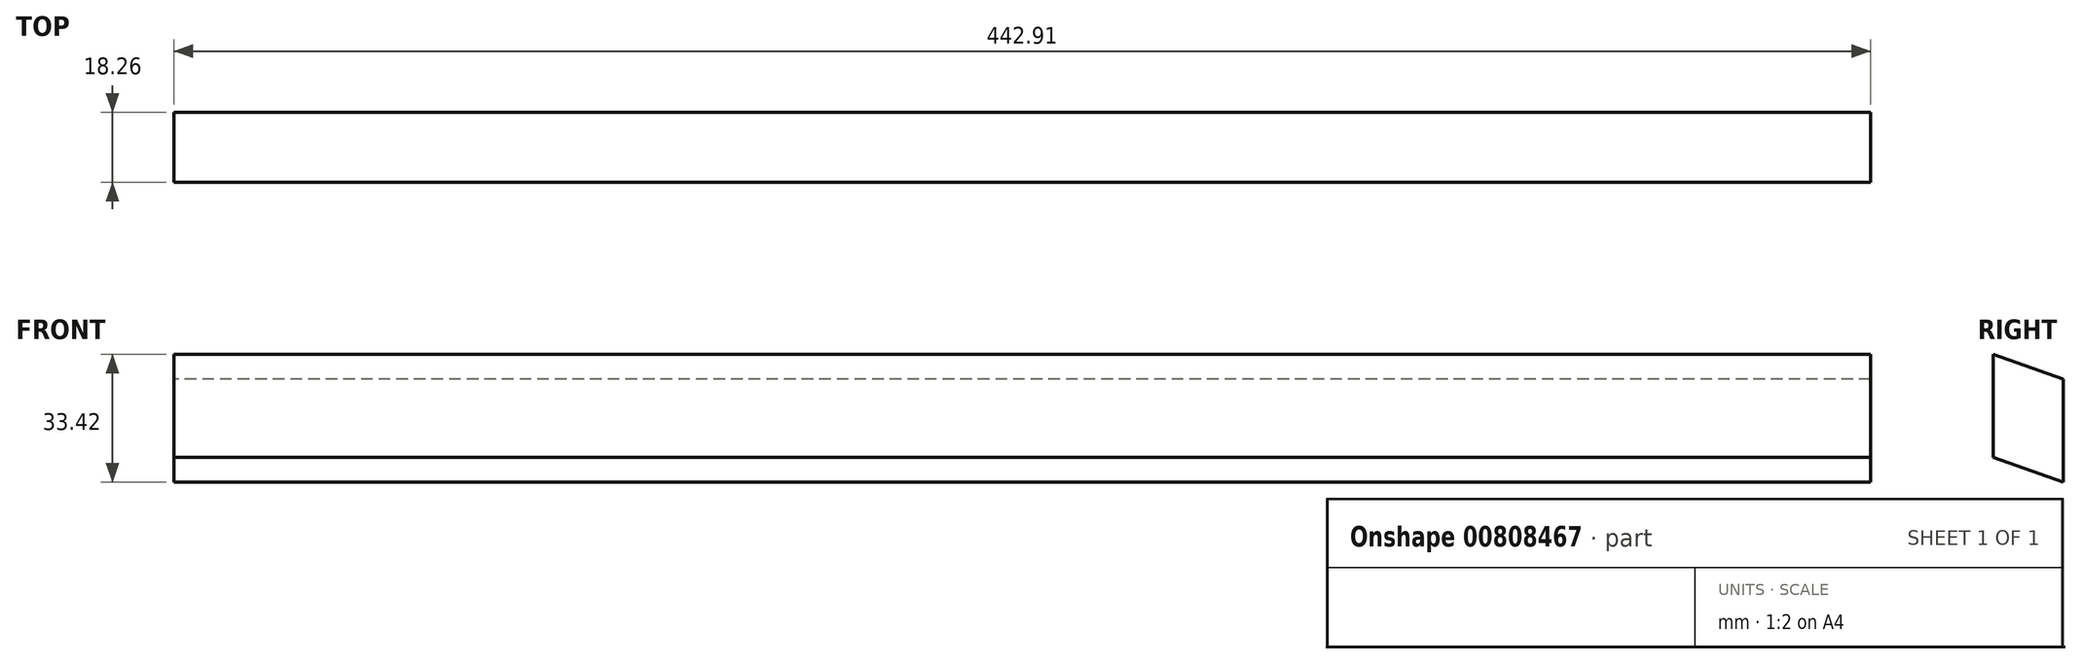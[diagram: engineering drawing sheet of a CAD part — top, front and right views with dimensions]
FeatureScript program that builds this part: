
annotation { "Feature Type Name" : "Feature", "Feature Type Description" : "" }
export const myFeature = defineFeature(function(context is Context, id is Id, definition is map)
    precondition{}
    {
        {
            var Q0;
            Q0=qCreatedBy(makeId("Right.planeOp"),FACE);
            var sketch = newSketch(context, id + "F0", { "sketchPlane" : qUnion([Q0])});
            skLineSegment(sketch, "E0", {"start": v(-140.85, 19.98) * mm, "end": v(-140.85, -81.62) * mm});
            skLineSegment(sketch, "E1", {"start": v(-140.85, -81.62) * mm, "end": v(145.7, -81.62) * mm});
            skLineSegment(sketch, "E2", {"start": v(145.7, -81.62) * mm, "end": v(-140.85, 19.98) * mm});
            skSolve(sketch);
        }
        {
            var Q0;
            Q0=qCreatedBy(makeId("Right.planeOp"),FACE);
            var sketch = newSketch(context, id + "F1", { "sketchPlane" : qUnion([Q0])});
            skLineSegment(sketch, "E3", {"start": v(-8.34, 14.4) * mm, "end": v(-8.34, -12.56) * mm});
            skLineSegment(sketch, "E4", {"start": v(-8.34, -12.56) * mm, "end": v(9.92, -19.03) * mm});
            skLineSegment(sketch, "E5", {"start": v(9.92, -19.03) * mm, "end": v(9.92, 7.92) * mm});
            skLineSegment(sketch, "E6", {"start": v(9.92, 7.92) * mm, "end": v(-8.34, 14.4) * mm});
            skSolve(sketch);
        }
        {
            var Q0;
            Q0 = qSketchRegion(id + "F1", true);
            extrude(context, id + "F2", {"entities" : qUnion([Q0]), "depth" : 442.91 * mm, "offsetDistance" : 25.4 * mm});
        }
    });
